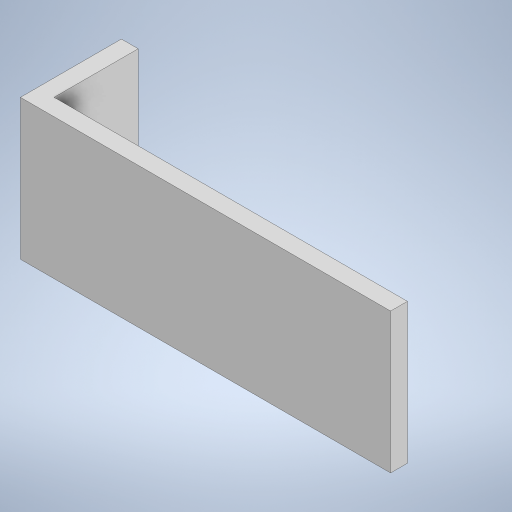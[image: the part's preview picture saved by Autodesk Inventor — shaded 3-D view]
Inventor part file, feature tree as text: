
AUTODESK INVENTOR PART (.ipt)
format: ipt  version: 2023 (Build 270158000, 158)  size: 211,456 bytes
history: native  units: in
note: dims shown in document units (in); Inventor stores cm internally (conversion verified against a paired STEP export)
features: extrude x2, sketch x2
ambient origin geometry x8: Origin, YZ Plane, XZ Plane, XY Plane, X Axis, Y Axis, Z Axis, Center Point
bodies: Solid1 (feature_tree)
feature tree (4):
  extrude  "Extrusion1"  Depth=0.9843in
  extrude  "Extrusion2"  Depth=0.7087in
  sketch  "Sketch1"  dims[d0=2.4803in d1=0.9843in]
  sketch  "Sketch2"  dims[d2=0.1181in d3=0.0in d4=0.7087in d5=0.1181in d6=0.0in]
